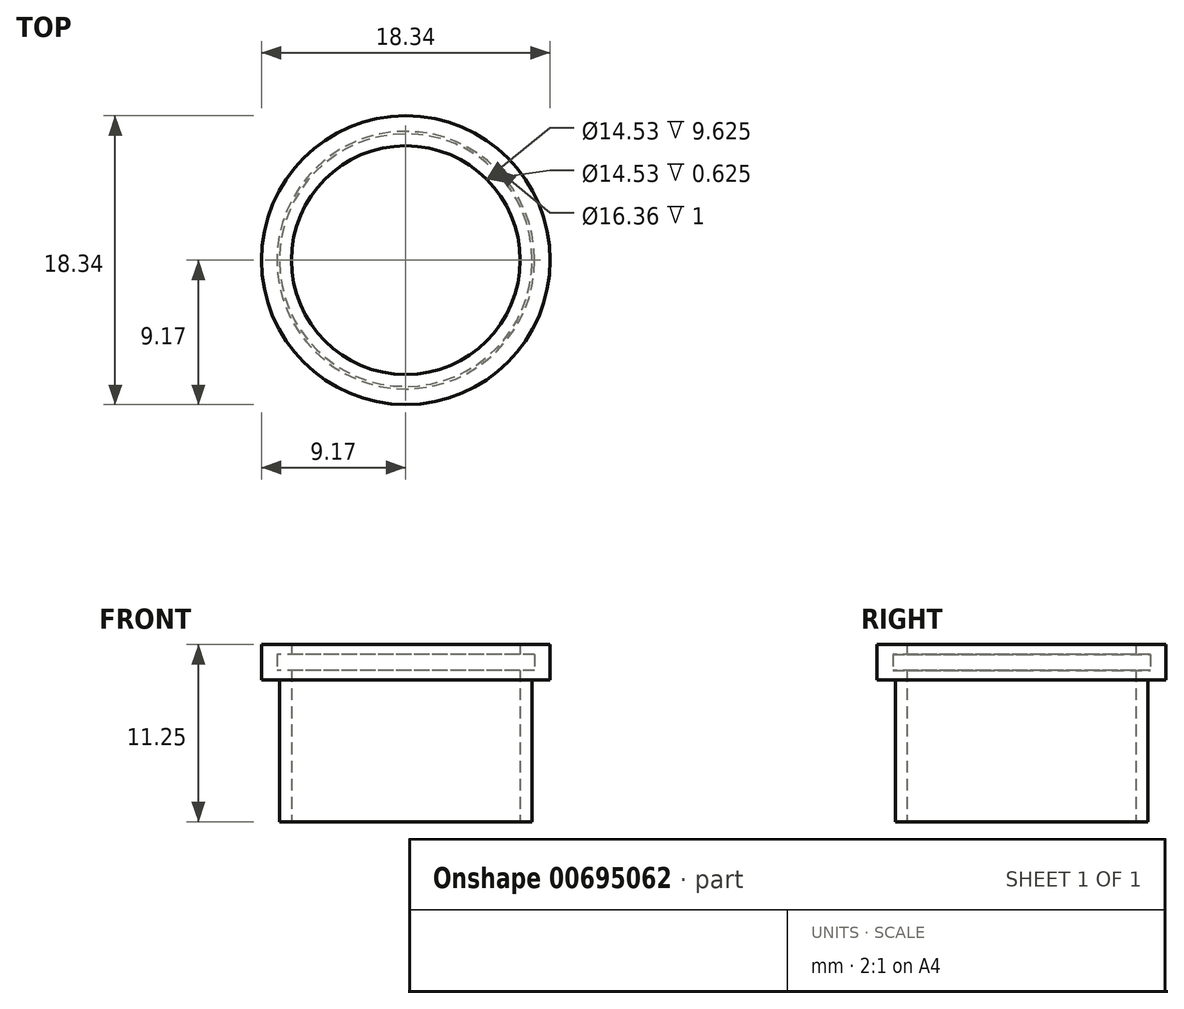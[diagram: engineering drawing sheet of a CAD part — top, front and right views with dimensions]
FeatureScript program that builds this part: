
annotation { "Feature Type Name" : "Feature", "Feature Type Description" : "" }
export const myFeature = defineFeature(function(context is Context, id is Id, definition is map)
    precondition{}
    {
        {
            var Q0;
            Q0=qCreatedBy(makeId("Top.planeOp"),FACE);
            var sketch = newSketch(context, id + "F0", { "sketchPlane" : qUnion([Q0])});
            skCircle(sketch, "E0", {"center": v(0, 0) * mm, "radius": 16.05 * mm});
            skCircle(sketch, "E1", {"center": v(0, 0) * mm, "radius": 18.34 * mm});
            skCircle(sketch, "E2", {"center": v(0, 0) * mm, "radius": 14.53 * mm});
            skSolve(sketch);
        }
        {
            var Q0;
            Q0=makeQuery(id+"F0.imprint","IMPRINT",FACE,{"disambiguationData":[TD([[makeQuery(id+"F0.imprint","IMPRINT",EDGE,{"derivedFrom":sQuery(id+"F0.wireOp",EDGE,"E0")}),1.0]])]});
            extrude(context, id + "F1", {"entities" : qUnion([Q0]), "depth" : 20 * mm, "offsetDistance" : 25 * mm});
        }
        {
            var Q0;
            Q0=makeQuery(id+"F0.imprint","IMPRINT",FACE,{"disambiguationData":[TD([[makeQuery(id+"F0.imprint","IMPRINT",EDGE,{"derivedFrom":sQuery(id+"F0.wireOp",EDGE,"E0")}),-1.0]])]});
            var Q1;
            Q1=makeQuery(id+"F0.imprint","IMPRINT",FACE,{"disambiguationData":[TD([[makeQuery(id+"F0.imprint","IMPRINT",EDGE,{"derivedFrom":sQuery(id+"F0.wireOp",EDGE,"E0")}),1.0]])]});
            extrude(context, id + "F2", {"entities" : qUnion([Q0, Q1]), "operationType" : NewBodyOperationType.ADD, "depth" : 22.5 * mm, "offsetDistance" : 25 * mm, "hasSecondDirection" : true, "secondDirectionOppositeDirection" : false, "secondDirectionDepth" : 18 * mm});
        }
        {
            var Q0;
            Q0=makeQuery(id+"F1.opExtrude","SWEPT_BODY",BODY,{"disambiguationData":[OSD([sQuery(id+"F0.wireOp",EDGE,"E0"),sQuery(id+"F0.wireOp",EDGE,"E2")])]});
            var Q1;
            Q1=sQuery(id+"F0.wireOp",VERTEX,"E0.center");
            transform(context, id + "F3", {"entities" : qUnion([Q0]), "transformType" : TransformType.SCALE_UNIFORMLY, "scale" : 0.5, "scalePoint" : qUnion([Q1]), "makeCopy" : false});
        }
        {
            var Q0;
            Q0=makeQuery(id+"F2.opExtrude","CAP_FACE",FACE,{"disambiguationData":[OSD([sQuery(id+"F0.wireOp",EDGE,"E1"),sQuery(id+"F0.wireOp",EDGE,"E2")])],"isStart":false});
            cPlane(context, id + "F4", {"entities" : qUnion([Q0]), "cplaneType" : CPlaneType.OFFSET, "offset" : (4.5 / 4) * mm, "oppositeDirection" : true, "width" : 150 * mm, "height" : 150 * mm});
        }
        {
            var Q0;
            Q0=qCreatedBy(id+"F4.planeOp",FACE);
            var sketch = newSketch(context, id + "F5", { "sketchPlane" : qUnion([Q0])});
            skCircle(sketch, "E3", {"center": v(0, 0) * mm, "radius": 8.18 * mm});
            skSolve(sketch);
        }
        {
            var Q0;
            Q0 = qSketchRegion(id + "F5", true);
            extrude(context, id + "F6", {"entities" : qUnion([Q0]), "operationType" : NewBodyOperationType.REMOVE, "depth" : 0.5 * mm, "offsetDistance" : 25 * mm, "hasSecondDirection" : true, "secondDirectionOppositeDirection" : true, "secondDirectionDepth" : 0.5 * mm});
        }
    });
